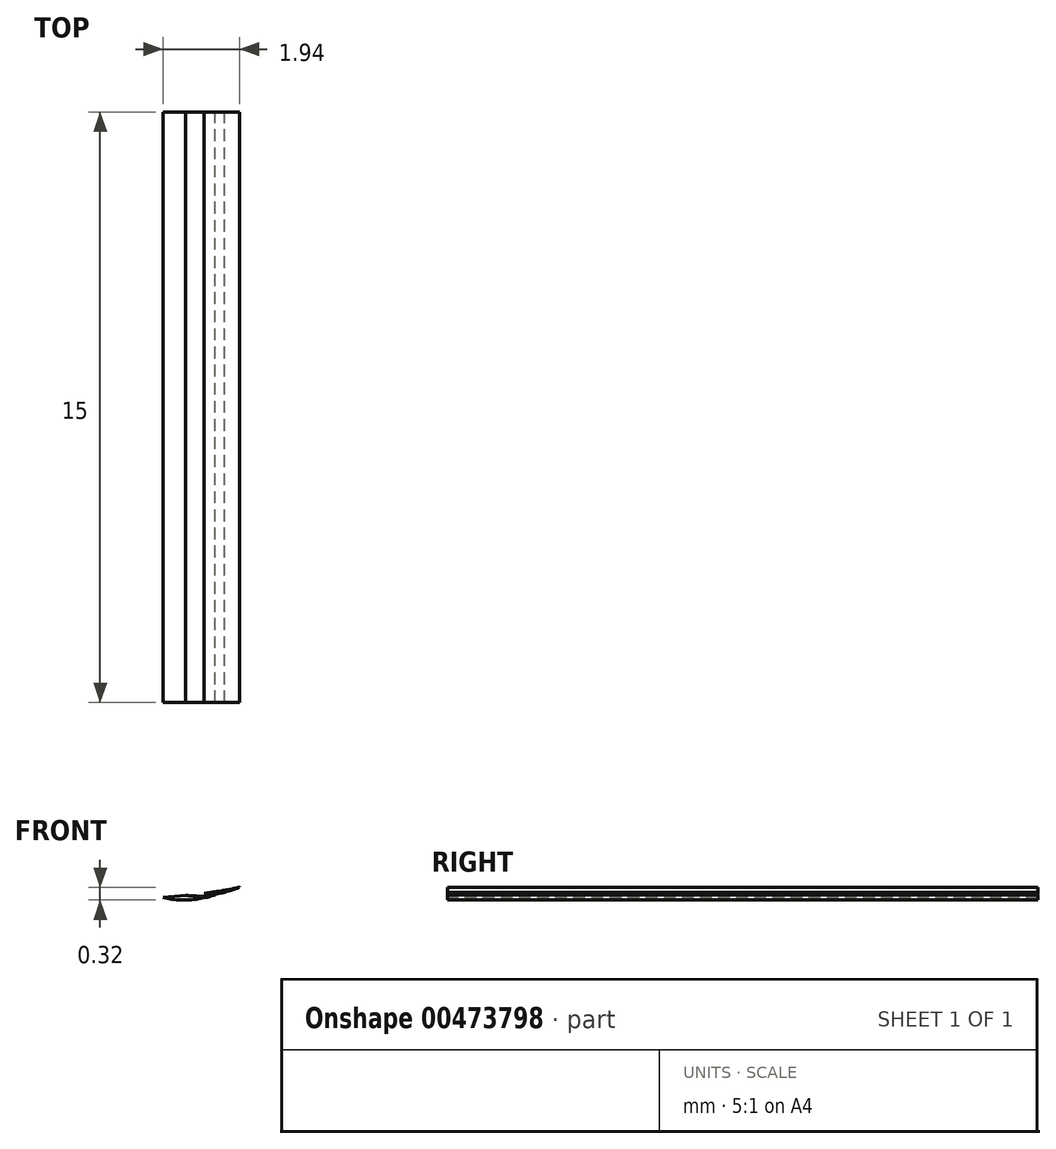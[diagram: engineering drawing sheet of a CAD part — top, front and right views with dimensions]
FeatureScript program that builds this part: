
annotation { "Feature Type Name" : "Feature", "Feature Type Description" : "" }
export const myFeature = defineFeature(function(context is Context, id is Id, definition is map)
    precondition{}
    {
        {
            var Q0;
            Q0=qCreatedBy(makeId("Front.planeOp"),FACE);
            var sketch = newSketch(context, id + "F0", { "sketchPlane" : qUnion([Q0])});
            skFitSpline(sketch, "E0", {"points": [v(-15.47, 23.12) * mm, v(-17, 22.61) * mm, v(-18.27, 21.94) * mm, v(-19.5, 20.9) * mm, v(-20.82, 19.2) * mm, v(-26.21, 8.6) * mm, v(-27.05, 7.1) * mm, v(-27.68, 6.24) * mm, v(-29.53, 4.96) * mm, v(-31.11, 4.18) * mm, v(-33.24, 3.87) * mm], "startDerivative": vector(-19.15, -5.66) * mm, "endDerivative": vector(-23.6, -2.3) * mm});
            skFitSpline(sketch, "E1", {"points": [v(-15.34, 22.23) * mm, v(-16.68, 21.68) * mm, v(-18.01, 20.74) * mm, v(-19, 19.86) * mm, v(-24.97, 8.28) * mm, v(-26.12, 6.27) * mm, v(-26.92, 5.28) * mm, v(-28.93, 3.94) * mm, v(-30.74, 3.16) * mm, v(-32.65, 2.92) * mm], "startDerivative": vector(-15.82, -5) * mm, "endDerivative": vector(-20.08, -1.27) * mm});
            skFitSpline(sketch, "E2", {"points": [v(-9.69, 21.63) * mm, v(-10.95, 21.9) * mm, v(-12.59, 22.1) * mm, v(-14.98, 22.13) * mm, v(-17.06, 21.36) * mm, v(-19, 19.86) * mm], "startDerivative": vector(-7.63, 1.9) * mm, "endDerivative": vector(-8.5, -7.34) * mm});
            skFitSpline(sketch, "E3", {"points": [v(-32.65, 2.92) * mm, v(-31.81, 2.55) * mm, v(-30.05, 2.26) * mm, v(-28.46, 2.38) * mm, v(-26.93, 2.8) * mm, v(-25.27, 3.63) * mm, v(-23.23, 4.95) * mm, v(-21.05, 7.01) * mm, v(-19.15, 9.14) * mm], "startDerivative": vector(8.61, -4.56) * mm, "endDerivative": vector(12.15, 14.06) * mm});
            skFitSpline(sketch, "E4", {"points": [v(-19.15, 9.14) * mm, v(-18.95, 9.37) * mm, v(-18.64, 9.34) * mm, v(-18.26, 9.14) * mm, v(-18.25, 8.93) * mm], "startDerivative": vector(0.74, 1.16) * mm, "endDerivative": vector(-0.24, -1.07) * mm});
            skFitSpline(sketch, "E5", {"points": [v(-18.25, 8.93) * mm, v(-18.37, 8.52) * mm, v(-18.67, 7.61) * mm, v(-19.02, 6.39) * mm, v(-19.07, 5.7) * mm, v(-18.6, 4.3) * mm, v(-18.03, 3.04) * mm, v(-17.33, 2.1) * mm, v(-16.55, 1.83) * mm, v(-15.62, 1.8) * mm, v(-15, 1.96) * mm, v(-14.33, 2.24) * mm], "startDerivative": vector(-1.76, -6.14) * mm, "endDerivative": vector(8.4, 3.86) * mm});
            skFitSpline(sketch, "E6", {"points": [v(-14.38, 2.43) * mm, v(-15.14, 2.43) * mm, v(-15.5, 2.5) * mm, v(-15.72, 2.77) * mm, v(-16.03, 3.23) * mm, v(-16.3, 3.78) * mm, v(-16.56, 4.6) * mm, v(-16.58, 5.55) * mm, v(-16.5, 6.47) * mm, v(-16.1, 7.64) * mm, v(-15.8, 8.42) * mm, v(-15.5, 9.86) * mm, v(-14.97, 10.98) * mm, v(-13.99, 11.63) * mm, v(-13.4, 11.46) * mm, v(-12.75, 10.7) * mm, v(-12.38, 9.53) * mm, v(-12.43, 8.56) * mm, v(-12.8, 7.37) * mm, v(-13.02, 6.33) * mm, v(-12.9, 4.82) * mm, v(-12.42, 3.72) * mm, v(-11.77, 2.92) * mm, v(-10.83, 2.3) * mm, v(-10.01, 2.08) * mm, v(-9.15, 2.1) * mm, v(-8.01, 2.31) * mm, v(-7.46, 2.43) * mm], "startDerivative": vector(-24.6, -0.27) * mm, "endDerivative": vector(17, 3.7) * mm});
            skFitSpline(sketch, "E7", {"points": [v(-14.1, 10.37) * mm, v(-14, 10.49) * mm, v(-13.9, 10.53) * mm, v(-13.74, 10.5) * mm, v(-13.59, 10.37) * mm], "startDerivative": vector(0.37, 0.52) * mm, "endDerivative": vector(0.52, -0.52) * mm});
            skFitSpline(sketch, "E8", {"points": [v(-7.46, 3.72) * mm, v(-8.3, 3.97) * mm, v(-8.78, 4.18) * mm, v(-9.14, 4.52) * mm, v(-9.65, 5.35) * mm, v(-9.77, 6.16) * mm, v(-9.74, 6.98) * mm, v(-8.9, 9.7) * mm, v(-8.83, 10.37) * mm], "startDerivative": vector(-7.4, 2.04) * mm, "endDerivative": vector(-0.15, 4.84) * mm});
            skFitSpline(sketch, "E9", {"points": [v(-7.74, 2.84) * mm, v(-8.15, 3) * mm, v(-8.66, 3.1) * mm, v(-9.04, 3.15) * mm, v(-9.74, 3.67) * mm, v(-10.28, 4.3) * mm, v(-10.64, 5.1) * mm, v(-10.82, 6.58) * mm, v(-10.69, 7.32) * mm, v(-10.07, 9.48) * mm, v(-9.8, 10.16) * mm, v(-9.57, 11.4) * mm, v(-9.49, 12.95) * mm], "startDerivative": vector(-6.75, 2.89) * mm, "endDerivative": vector(0.41, 14.38) * mm});
            skFitSpline(sketch, "E10", {"points": [v(-9.49, 12.95) * mm, v(-9.03, 12.95) * mm], "startDerivative": vector(0.46, 0) * mm, "endDerivative": vector(0.46, 0) * mm});
            skFitSpline(sketch, "E11", {"points": [v(-9.03, 12.95) * mm, v(-7.23, 9.7) * mm, v(-7.11, 9.6) * mm, v(-6.98, 10.02) * mm, v(-6.98, 10.99) * mm, v(-7.2, 11.8) * mm, v(-7.58, 13.22) * mm, v(-7.62, 14.03) * mm, v(-7.24, 14.53) * mm, v(-6.61, 14.74) * mm, v(-6.06, 14.6) * mm, v(-3.57, 11.04) * mm], "startDerivative": vector(13.69, -25.43) * mm, "endDerivative": vector(15.82, -25.66) * mm});
            skFitSpline(sketch, "E12", {"points": [v(-8.83, 10.37) * mm, v(-8.83, 10.64) * mm, v(-8.74, 10.64) * mm, v(-8.63, 10.47) * mm, v(-7.9, 9.2) * mm, v(-7.53, 8.94) * mm, v(-7.05, 8.84) * mm, v(-6.55, 9.08) * mm, v(-6.11, 9.82) * mm, v(-6.06, 10.93) * mm, v(-6.17, 11.8) * mm, v(-6.57, 13.15) * mm, v(-6.69, 13.58) * mm, v(-6.67, 13.78) * mm, v(-6.56, 13.82) * mm, v(-6.44, 13.78) * mm, v(-4.52, 11.04) * mm, v(-4.55, 10.82) * mm, v(-5.05, 10.2) * mm, v(-4.86, 9.93) * mm, v(-4.09, 9.35) * mm, v(-3, 9.17) * mm, v(-2.58, 9.3) * mm, v(-2.16, 9.33) * mm, v(-2, 11.6) * mm, v(-2.17, 12.71) * mm, v(-2.65, 13.6) * mm, v(-3.25, 14.46) * mm, v(-3.57, 15.49) * mm, v(-2.36, 17.35) * mm, v(-2.06, 19.44) * mm, v(-2.34, 22.37) * mm, v(-2.53, 24.33) * mm, v(-2.5, 26.48) * mm, v(-2.37, 27.94) * mm, v(-2.64, 29) * mm, v(-3.83, 30.53) * mm, v(-5.3, 31.23) * mm, v(-7.01, 31.27) * mm], "startDerivative": vector(-3.8, 25.12) * mm, "endDerivative": vector(-49.58, -2.47) * mm});
            skFitSpline(sketch, "E13", {"points": [v(-3.57, 11.04) * mm, v(-3.46, 10.84) * mm, v(-3.86, 10.45) * mm, v(-3.98, 10.28) * mm, v(-3.9, 10.16) * mm, v(-3.43, 10.03) * mm, v(-2.86, 10.02) * mm, v(-2.77, 10.16) * mm, v(-2.8, 11.66) * mm, v(-3, 12.46) * mm, v(-3.57, 13.37) * mm, v(-3.95, 13.9) * mm, v(-4.43, 15.02) * mm, v(-4.54, 15.5) * mm, v(-4.5, 15.98) * mm, v(-3.68, 17.26) * mm, v(-3.3, 17.92) * mm, v(-3.03, 19.2) * mm, v(-3.06, 20.27) * mm], "startDerivative": vector(5.82, -5.76) * mm, "endDerivative": vector(-1.27, 14.3) * mm});
            skFitSpline(sketch, "E14", {"points": [v(-3.06, 20.27) * mm, v(-3.58, 24.17) * mm, v(-3.66, 25.35) * mm, v(-3.56, 26.82) * mm, v(-3.45, 27.79) * mm, v(-3.89, 28.78) * mm, v(-4.7, 29.72) * mm, v(-5.52, 30.2) * mm, v(-6.63, 30.3) * mm], "startDerivative": vector(-2.96, 21.6) * mm, "endDerivative": vector(-10.44, 0) * mm});
            skFitSpline(sketch, "E15", {"points": [v(-9.69, 21.63) * mm, v(-8.77, 21.5) * mm, v(-7.81, 21.55) * mm, v(-6.94, 22.4) * mm, v(-6.61, 24.5) * mm, v(-6.81, 25.9) * mm], "startDerivative": vector(5.33, -0.9) * mm, "endDerivative": vector(-1.28, 6.15) * mm});
            skFitSpline(sketch, "E16", {"points": [v(-6.81, 25.9) * mm, v(-9.8, 25.9) * mm, v(-11.73, 26.35) * mm, v(-12.9, 27.08) * mm, v(-12.85, 28.72) * mm, v(-10.2, 30.46) * mm, v(-8.2, 31.1) * mm, v(-7.01, 31.27) * mm], "startDerivative": vector(-18.05, -0.82) * mm, "endDerivative": vector(10.4, 1.03) * mm});
            skFitSpline(sketch, "E17", {"points": [v(-15.47, 23.12) * mm, v(-14.22, 23.24) * mm, v(-12.58, 23.22) * mm, v(-9.81, 22.8) * mm, v(-8.9, 22.74) * mm, v(-8.04, 23.01) * mm, v(-7.87, 23.42) * mm, v(-8.28, 23.68) * mm, v(-9.14, 23.95) * mm], "startDerivative": vector(9.17, 1.06) * mm, "endDerivative": vector(-7.85, 2.42) * mm});
            skFitSpline(sketch, "E18", {"points": [v(-8.04, 23.01) * mm, v(-7.68, 23.87) * mm, v(-7.7, 25.87) * mm], "startDerivative": vector(1.07, 1.87) * mm, "endDerivative": vector(-0.31, 3.72) * mm});
            skFitSpline(sketch, "E19", {"points": [v(-6.63, 30.3) * mm, v(-7.76, 30.1) * mm, v(-9.62, 29.62) * mm, v(-11.4, 28.68) * mm, v(-11.7, 27.73) * mm, v(-9.82, 26.94) * mm, v(-7.15, 26.78) * mm, v(-6.81, 25.9) * mm], "startDerivative": vector(-8.95, -1.51) * mm, "endDerivative": vector(0.83, -10.1) * mm});
            skLineSegment(sketch, "E20", {"start": v(-15.83, 0.64) * mm, "end": v(1.46, 0.64) * mm});
            skFitSpline(sketch, "E21", {"points": [v(-13.59, 10.37) * mm, v(-13.37, 9.68) * mm, v(-13.32, 8.89) * mm, v(-13.85, 7.1) * mm, v(-14, 5.86) * mm, v(-13.86, 4.68) * mm, v(-13.28, 3.36) * mm, v(-12.37, 1.92) * mm], "startDerivative": vector(2.11, -6.44) * mm, "endDerivative": vector(5.74, -8.65) * mm});
            skPoint(sketch, "E22.4.internal.snap0", {"position": v(-7.19, 0.64) * mm});
            skFitSpline(sketch, "E22", {"points": [v(-12.37, 1.92) * mm, v(-11.87, 1.31) * mm, v(-11.03, 0.9) * mm, v(-9.4, 0.64) * mm, v(-7.19, 0.75) * mm, v(-6.17, 1.1) * mm, v(-5.72, 1.49) * mm, v(-5.5, 2.09) * mm, v(-5.72, 2.83) * mm, v(-7.46, 3.72) * mm], "startDerivative": vector(4.86, -7) * mm, "endDerivative": vector(-14.47, 5.4) * mm});
            skFitSpline(sketch, "E23", {"points": [v(-20.3, 6.34) * mm, v(-20.02, 4.84) * mm, v(-19.44, 3.27) * mm, v(-18.59, 1.66) * mm, v(-17.6, 0.9) * mm, v(-15.83, 0.64) * mm, v(-14.3, 0.77) * mm, v(-13.5, 1.23) * mm, v(-13.08, 1.85) * mm, v(-13.11, 2.52) * mm, v(-13.55, 3.26) * mm, v(-14.35, 3.43) * mm, v(-14.96, 3.44) * mm, v(-15.38, 4) * mm, v(-15.66, 4.87) * mm, v(-15.7, 6.18) * mm, v(-15, 8.07) * mm, v(-14.63, 9.25) * mm, v(-14.39, 9.96) * mm, v(-14.1, 10.37) * mm], "startDerivative": vector(3.64, -24.3) * mm, "endDerivative": vector(8.5, 10.55) * mm});
            skLineSegment(sketch, "E24", {"start": v(-15.83, 0.64) * mm, "end": v(-38.68, 0.64) * mm});
            skFitSpline(sketch, "E25", {"points": [v(-20.3, 6.34) * mm, v(-21.41, 4.95) * mm, v(-22.8, 3.73) * mm, v(-24.9, 2.47) * mm, v(-27.4, 1.43) * mm, v(-29.62, 0.9) * mm, v(-32.37, 0.64) * mm, v(-35.19, 0.8) * mm, v(-36.69, 1.17) * mm], "startDerivative": vector(-9.58, -12.94) * mm, "endDerivative": vector(-13.21, 3.94) * mm});
            skFitSpline(sketch, "E26", {"points": [v(-29.53, 4.96) * mm, v(-30.24, 4.59) * mm, v(-30.81, 4.33) * mm, v(-31.69, 4) * mm, v(-32.4, 4.04) * mm, v(-33.34, 5.2) * mm, v(-34.07, 8.07) * mm], "startDerivative": vector(-5.36, -2.74) * mm, "endDerivative": vector(-2.07, 11.59) * mm});
            skFitSpline(sketch, "E27", {"points": [v(-36.7, 2.56) * mm, v(-35.86, 1.89) * mm, v(-33.81, 1.38) * mm, v(-31.33, 1.56) * mm, v(-29.08, 2.03) * mm, v(-26.93, 2.8) * mm], "startDerivative": vector(4.8, -4.93) * mm, "endDerivative": vector(10, 3.98) * mm});
            skFitSpline(sketch, "E28", {"points": [v(-36.69, 1.17) * mm, v(-37.5, 1.58) * mm, v(-37.97, 1.97) * mm, v(-38.4, 2.65) * mm, v(-38.64, 3.56) * mm, v(-38.8, 5.34) * mm, v(-38, 6.85) * mm, v(-36.32, 7.39) * mm, v(-35, 7.09) * mm, v(-34.27, 5.67) * mm, v(-33.75, 4.29) * mm, v(-33.24, 3.87) * mm, v(-32.38, 3.83) * mm, v(-31.69, 4) * mm], "startDerivative": vector(-12.72, 5.88) * mm, "endDerivative": vector(10.73, 3.35) * mm});
            skFitSpline(sketch, "E29.trimOffspring", {"points": [v(-20.3, 6.34) * mm, v(-20.02, 4.84) * mm, v(-19.44, 3.27) * mm, v(-18.59, 1.66) * mm, v(-17.6, 0.9) * mm, v(-15.83, 0.64) * mm, v(-14.3, 0.77) * mm, v(-13.5, 1.23) * mm, v(-13.08, 1.85) * mm, v(-13.11, 2.52) * mm, v(-13.55, 3.26) * mm, v(-14.35, 3.43) * mm, v(-14.96, 3.44) * mm, v(-15.38, 4) * mm, v(-15.66, 4.87) * mm, v(-15.7, 6.18) * mm, v(-15, 8.07) * mm, v(-14.63, 9.25) * mm, v(-14.39, 9.96) * mm, v(-14.1, 10.37) * mm], "startDerivative": vector(3.64, -24.3) * mm, "endDerivative": vector(8.5, 10.55) * mm});
            skFitSpline(sketch, "E30", {"points": [v(-13.08, 1.85) * mm, v(-13.21, 1.5) * mm, v(-13.53, 1.06) * mm, v(-13.85, 0.8) * mm, v(-14.19, 0.64) * mm], "startDerivative": vector(-0.42, -1.46) * mm, "endDerivative": vector(-1.48, -0.58) * mm});
            skLineSegment(sketch, "E31", {"start": v(-14.19, 0.64) * mm, "end": v(-18.28, 0.64) * mm});
            skFitSpline(sketch, "E32", {"points": [v(-18.28, 0.64) * mm, v(-18.6, 0.76) * mm, v(-18.83, 0.97) * mm, v(-19.3, 1.95) * mm, v(-19.6, 2.93) * mm, v(-20.3, 6.34) * mm], "startDerivative": vector(-2.98, 0.9) * mm, "endDerivative": vector(-2.11, 10.81) * mm});
            skFitSpline(sketch, "E33", {"points": [v(-28.93, 3.94) * mm, v(-29.77, 3.54) * mm, v(-31.34, 3.02) * mm, v(-33.12, 2.8) * mm, v(-34.05, 2.84) * mm, v(-35.14, 3.27) * mm, v(-36.14, 4.21) * mm, v(-36.56, 5.13) * mm, v(-36.71, 5.8) * mm], "startDerivative": vector(-6.95, -3.48) * mm, "endDerivative": vector(-1.27, 6.72) * mm});
            skFitSpline(sketch, "E34", {"points": [v(-36.7, 2.56) * mm, v(-37.01, 3.08) * mm, v(-37.24, 3.85) * mm, v(-37.26, 5.03) * mm, v(-36.83, 6.27) * mm], "startDerivative": vector(-1.71, 2.46) * mm, "endDerivative": vector(1.84, 4.18) * mm});
            skLineSegment(sketch, "E35", {"start": v(-36.71, 5.8) * mm, "end": v(-36.83, 6.27) * mm});
            skFitSpline(sketch, "E36", {"points": [v(-5.5, 2.09) * mm, v(-5.56, 1.84) * mm, v(-5.67, 1.6) * mm, v(-5.84, 1.33) * mm, v(-6.12, 0.98) * mm, v(-6.37, 0.79) * mm, v(-6.64, 0.64) * mm], "startDerivative": vector(-0.4, -1.65) * mm, "endDerivative": vector(-1.72, -0.85) * mm});
            skLineSegment(sketch, "E37", {"start": v(-6.64, 0.64) * mm, "end": v(-11.25, 0.64) * mm});
            skFitSpline(sketch, "E38", {"points": [v(-11.25, 0.64) * mm, v(-11.44, 0.76) * mm, v(-11.77, 1.08) * mm, v(-12.17, 1.58) * mm, v(-12.37, 1.92) * mm], "startDerivative": vector(-0.99, 0.51) * mm, "endDerivative": vector(-0.72, 1.3) * mm});
            skFitSpline(sketch, "E39", {"points": [v(-15.72, 2.77) * mm, v(-15.59, 2.65) * mm, v(-15.17, 2.57) * mm, v(-14.68, 2.57) * mm, v(-14.14, 2.54) * mm, v(-13.96, 2.36) * mm, v(-14.03, 2.08) * mm, v(-14.3, 1.9) * mm, v(-14.9, 1.68) * mm, v(-15.87, 1.58) * mm, v(-16.34, 1.62) * mm, v(-16.9, 1.77) * mm, v(-17.28, 1.94) * mm, v(-17.64, 2.33) * mm, v(-18.03, 3.04) * mm], "startDerivative": vector(2.48, -2.83) * mm, "endDerivative": vector(-4, 8.14) * mm});
            skFitSpline(sketch, "E40", {"points": [v(-9.74, 3.67) * mm, v(-9.5, 3.5) * mm, v(-9.04, 3.37) * mm, v(-8.45, 3.23) * mm, v(-7.92, 3.09) * mm, v(-7.5, 2.92) * mm, v(-7.26, 2.64) * mm, v(-7.26, 2.28) * mm, v(-7.47, 2.09) * mm, v(-8.01, 2) * mm, v(-9.04, 2) * mm, v(-10.01, 2.08) * mm], "startDerivative": vector(3.08, -2.54) * mm, "endDerivative": vector(-7.55, 0.94) * mm});
            skFitSpline(sketch, "E41", {"points": [v(-38.8, 5.34) * mm, v(-38.72, 6.1) * mm, v(-38.54, 6.57) * mm, v(-38.18, 7) * mm, v(-37.65, 7.36) * mm, v(-37.02, 7.55) * mm, v(-36.25, 7.62) * mm, v(-35.7, 7.61) * mm, v(-35.13, 7.5) * mm, v(-34.58, 6.87) * mm, v(-34.12, 5.7) * mm, v(-33.8, 4.69) * mm, v(-33.6, 4.27) * mm, v(-33.46, 4.06) * mm, v(-33.24, 3.87) * mm], "startDerivative": vector(0.57, 10.4) * mm, "endDerivative": vector(4.93, -3.64) * mm});
            skFitSpline(sketch, "E42", {"points": [v(-34.12, 5.7) * mm, v(-33.86, 4.9) * mm, v(-33.69, 4.54) * mm, v(-33.59, 4.42) * mm, v(-33.4, 4.22) * mm, v(-33.2, 4.08) * mm, v(-32.88, 3.96) * mm, v(-32.4, 3.9) * mm, v(-32.09, 3.91) * mm, v(-31.97, 3.93) * mm, v(-31.92, 3.94) * mm], "startDerivative": vector(1.5, -5.08) * mm, "endDerivative": vector(1.09, 0.22) * mm});
            skSolve(sketch);
        }
        {
            var Q0;
            Q0=makeQuery(id+"F0.imprint","IMPRINT",FACE,{"disambiguationData":[TD([[makeQuery(id+"F0.imprint","IMPRINT",EDGE,{"derivedFrom":sQuery(id+"F0.wireOp",EDGE,"E0")}),1.0]])]});
            extrude(context, id + "F1", {"entities" : qUnion([Q0]), "depth" : 15 * mm});
        }
    });
